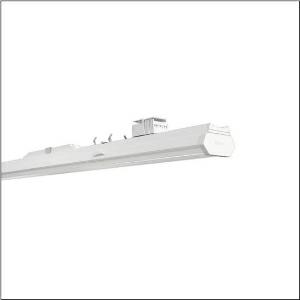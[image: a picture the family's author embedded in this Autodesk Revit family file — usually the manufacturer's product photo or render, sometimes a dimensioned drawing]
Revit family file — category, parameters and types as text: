
# Revit family: licross_r__21_protected_ho_52td12dn4dxm_7c2c
name_source: partatom
category: Lighting Fixtures
units: mm (PartAtom-declared; Revit-internal decimal feet)

## family parameters
Cut with Voids When Loaded = No
Host = Face
Light Source = No
Part Type = Normal
Room Calculation Point = No
Round Connector Dimension = Use Diameter
Shared = No

## types (1)
- --- (1 x LED, 13000 lm, 74.3 W, 4000K)
    Apparent Load = 74 VA
    CIE Flux Codes = 70 91 97 98 100
    Color Rendering = 80
    Color Temperature = 4000K
    Default Elevation = 1800 mm
    Description = Licross® 21 Protected HO, luminaire insert, of sheet steel, galvanised, coil coated, white, length: 1.500mm, width: 90mm, height: 103mm, LED rated luminous flux: 13.000lm, light colour: 840, control gear: DALI 2, with plug, 5-pole, with phase selection, mains connection: 220..240V, AC, 50/60Hz, rated input power: 74W, internal wiring halogen-free, primary light control with lens, of plastic, primary optical cover: cover, of PMMA, light emission: direct distribution, primary light characteristic: symmetric, protection rating (complete): IP54, insulation class (complete): insulation class I (protective earthing), certification: CE, ENEC, VDE, UKCA, protection symbol: D if used in an environment with non-conductive dust loads with corresponding accessories, impact resistance: IK06, permissible ambient temperature for indoor applications: -25..+40°C, corresponds to IFS (International Featured Standards) requirements for safety and quality in the food industry, reducing of maximum allowable ambient temperature of 5°C with ceiling mounting, LABS conformity tested according to VDMA 24364:2018-05, packaging unit: 1 piece
    Height = 92 mm
    Lamp = 1 x LED
    Lamp Light Flux = 13000 lm
    Lamp Power = 74.3 W
    Lamp count = 1
    Length = 1500 mm
    Luminous efficacy = 175 lm/W
    Manufacturer = Siteco
    ModVariant = No
    Model = 52TD12DN4DXM
    Mounting Place = Ceiling
    Mounting Type = Pendant
    Number of Poles = 1
    OnlyDefault = Yes
    Power Factor = 1
    Product Name = Licross® 21 Protected HO
    Product group = luminaire insert | ceiling pendant
    ProductGroupID = 902
    Protection Class = Protection class I
    Protection Degree = IP 54
    RLX_Detail_Level = 1
    RLX_Emergency_Light_Flux = 0 lm
    RLX_Emergency_Type = 0
    RLX_Emergency_Type_DB = No
    RlxData = <blob elided: 24457 chars, md5=988a0dcc>
    Socket = socket
    Standby Power = 0 W
    System Light Flux = 13000 lm
    System Power = 74 W
    Type Comments = factory setting: luminous flux: 100 % | dim-lin: 254 | 424 mA
    Type Image = l_1256148.jpg
    URL = http://relux.com
    VarID = @adj_150449
    Voltage = 0 V
    Weight = 0.00 kg
    Width = 88 mm

## geometry (parser evidence)
native form markers: Blend x4, Sweep x9
no freeform markers — native parametric forms only
